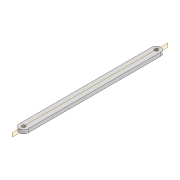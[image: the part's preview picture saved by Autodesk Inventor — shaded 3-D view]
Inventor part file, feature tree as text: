
AUTODESK INVENTOR PART (.ipt)
format: ipt  version: 2022 (Build 260153000, 153)  size: 86,528 bytes
history: native  units: mm
features: extrude x1, sketch x1
ambient origin geometry x8: Origin, YZ Plane, XZ Plane, XY Plane, X Axis, Y Axis, Z Axis, Center Point
bodies: Solid1 (feature_tree)
feature tree (2):
  extrude  "Extrusion1"  Depth=10.0mm
  sketch  "Sketch1"  dims[d0=150.0mm d1=10.0mm d2=4.0mm d3=4.0mm d4=4.0mm d5=0.0mm]
